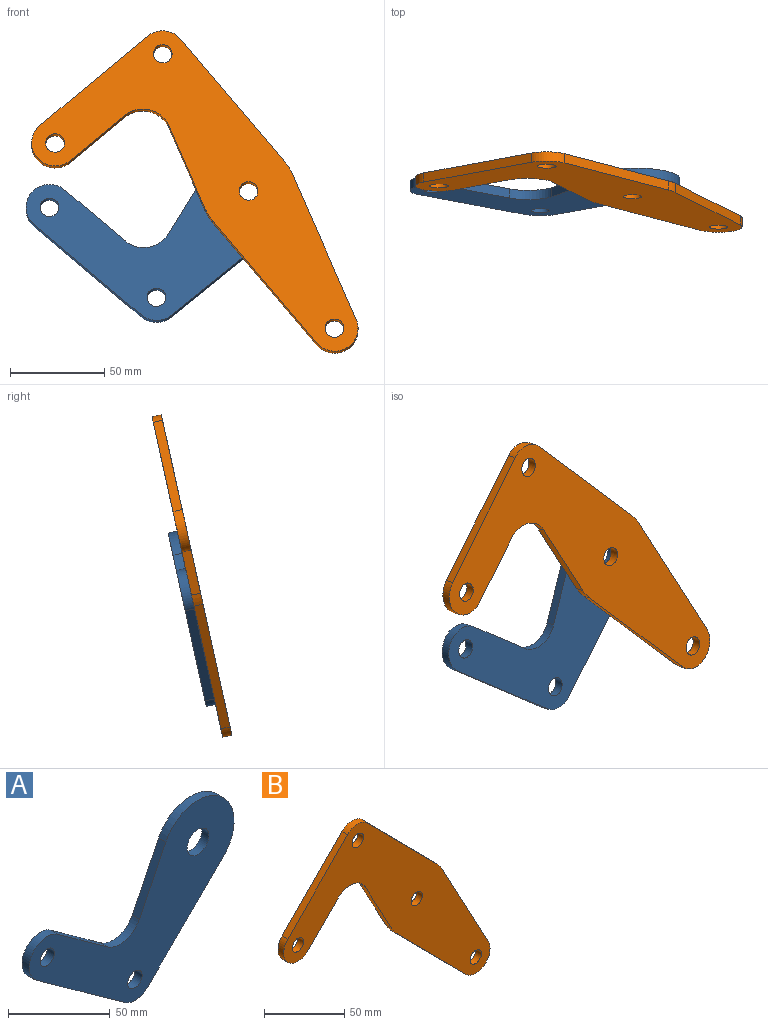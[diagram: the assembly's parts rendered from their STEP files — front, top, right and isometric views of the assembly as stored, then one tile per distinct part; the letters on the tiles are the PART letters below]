
ASSEMBLY  parts=2 mates=1
PART A: 13 faces, bbox 142.2x5x98.4 mm
  f0: cylinder r=25mm len=47.44mm, axis (0,-1,0), area 434.6mm2, adj f1,f8,f11,f12
  f1: plane 37.17x18.26mm, normal (-0.9,0,0.44), area 207.1mm2, adj f0,f2,f11,f12
  f2: cylinder r=15mm len=22.23mm, axis (0,-1,0), area 130.4mm2, adj f1,f3,f11,f12
  f3: plane 34.46x24.81mm, normal (0.58,0,0.81), area 212.3mm2, adj f2,f4,f11,f12
  f4: cylinder r=12.5mm len=22.64mm, axis (0,-1,0), area 196.3mm2, adj f3,f5,f11,f12
  f5: plane 60.86x43.82mm, normal (-0.58,0,-0.81), area 375mm2, adj f4,f6,f11,f12
  f6: cylinder r=12.5mm len=16.09mm, axis (0,-1,0), area 87.7mm2, adj f5,f8,f11,f12
  f7: cylinder r=5mm len=10mm, axis (0,-1,0), area 157.1mm2, adj f11,f12
  f8: plane 52.61x51.97mm, normal (0.7,0,-0.71), area 369.8mm2, adj f0,f6,f11,f12
  f9: cylinder r=7.5mm len=15mm, axis (0,-1,0), area 235.6mm2, adj f11,f12
  f10: cylinder r=5mm len=10mm, axis (0,-1,0), area 157.1mm2, adj f11,f12
  f11: plane 142.19x98.36mm, normal (0,1,0), area 5641.6mm2, adj f0,f1,f2,f3,f4,f5,f6,f7
  f12: plane 142.19x98.36mm, normal (0,-1,0), area 5641.6mm2, adj f0,f1,f2,f3,f4,f5,f6,f7
PART B: 18 faces, bbox 181.7x5x165.8 mm
  f0: plane 43.49x23.35mm, normal (-0.88,0,-0.47), area 246.8mm2, adj f1,f14,f16,f17
  f1: cylinder r=25mm len=5.75mm, axis (0,1,0), area 35.8mm2, adj f0,f2,f16,f17
  f2: plane 61.6x60.87mm, normal (-0.71,0,-0.7), area 433mm2, adj f1,f3,f16,f17
  f3: cylinder r=12.5mm len=21.39mm, axis (0,1,0), area 178.4mm2, adj f2,f4,f16,f17
  f4: plane 76.3x40.96mm, normal (0.88,0,0.47), area 433mm2, adj f3,f5,f16,f17
  f5: cylinder r=25mm len=5.75mm, axis (0,1,0), area 35.8mm2, adj f4,f6,f16,f17
  f6: plane 61.6x60.87mm, normal (0.71,0,0.7), area 433mm2, adj f5,f7,f16,f17
  f7: cylinder r=12.5mm len=17.78mm, axis (0,1,0), area 98.9mm2, adj f6,f8,f16,f17
  f8: plane 53.35x52.71mm, normal (-0.71,0,0.7), area 375mm2, adj f7,f9,f16,f17
  f9: cylinder r=12.5mm len=21.39mm, axis (0,1,0), area 196.3mm2, adj f8,f10,f16,f17
  f10: plane 26.86x26.54mm, normal (0.71,0,-0.7), area 188.8mm2, adj f9,f14,f16,f17
  f11: cylinder r=5mm len=10mm, axis (0,1,0), area 157.1mm2, adj f16,f17
  f12: cylinder r=5mm len=10mm, axis (0,1,0), area 157.1mm2, adj f16,f17
  f13: cylinder r=5mm len=10mm, axis (0,1,0), area 157.1mm2, adj f16,f17
  f14: cylinder r=15mm len=23.89mm, axis (0,1,0), area 140.2mm2, adj f0,f10,f16,f17
  f15: cylinder r=5mm len=10mm, axis (0,1,0), area 157.1mm2, adj f16,f17
  f16: plane 181.66x165.78mm, normal (0,-1,0), area 8710.1mm2, adj f0,f1,f2,f3,f4,f5,f6,f7
  f17: plane 181.66x165.78mm, normal (0,1,0), area 8710.1mm2, adj f0,f1,f2,f3,f4,f5,f6,f7
PLACE A rot(axis=(-0.93,0.37,-0.04),13.4deg) t=(55.78,-2.77,15.56)mm
PLACE B rot(axis=(-0.93,0.37,-0.04),13.4deg) t=(55.78,-2.77,15.56)mm
MATE revolute A.f0 <-> B.f1  axis (0,-0.98,0.22) through (55.78,-2.77,15.56)mm
